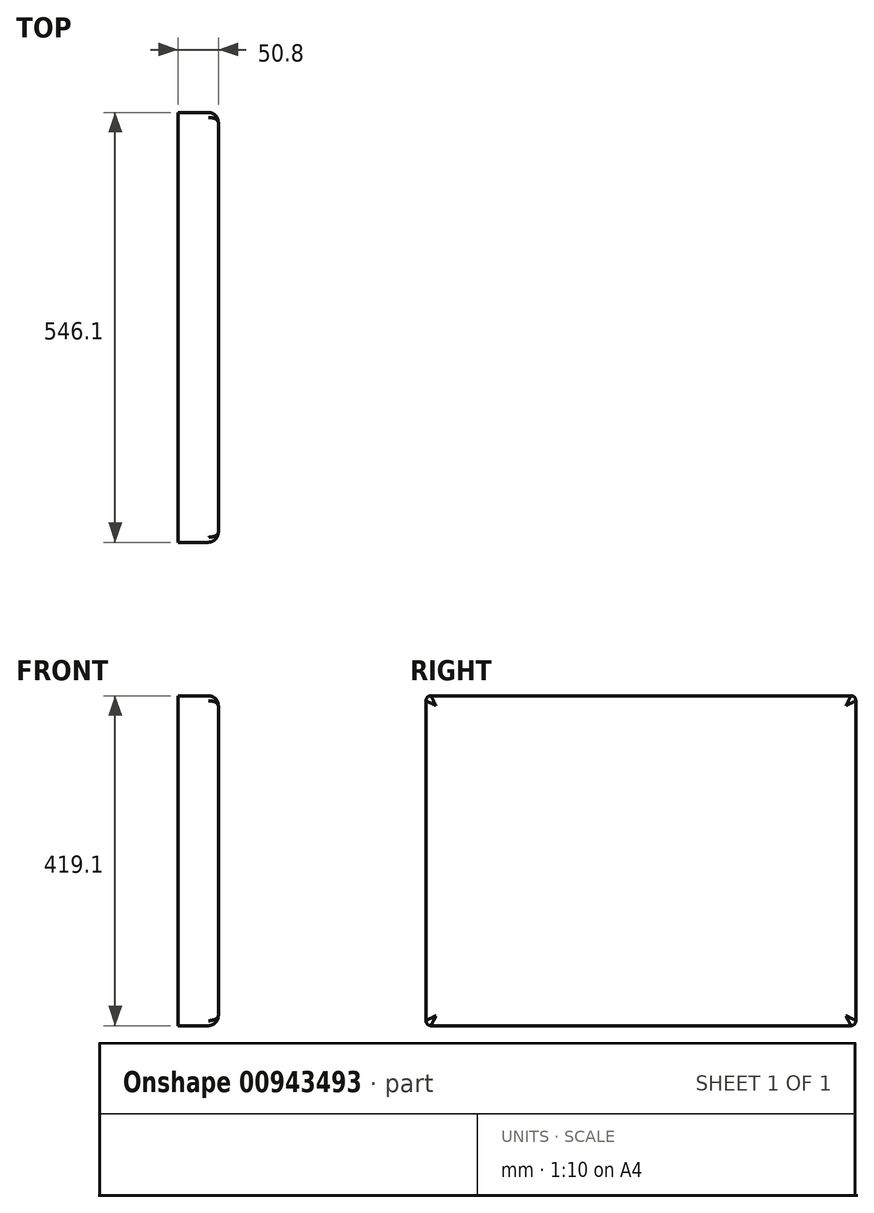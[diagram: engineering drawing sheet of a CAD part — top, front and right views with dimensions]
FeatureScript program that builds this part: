
annotation { "Feature Type Name" : "Feature", "Feature Type Description" : "" }
export const myFeature = defineFeature(function(context is Context, id is Id, definition is map)
    precondition{}
    {
        {
            var Q0;
            Q0=qCreatedBy(makeId("Right.planeOp"),FACE);
            var sketch = newSketch(context, id + "F0", { "sketchPlane" : qUnion([Q0])});
            skLineSegment(sketch, "E0.bottom", {"start": v(489.07, 13.05) * mm, "end": v(-44.33, 13.05) * mm});
            skLineSegment(sketch, "E0.top", {"start": v(489.07, 432.15) * mm, "end": v(-44.33, 432.15) * mm});
            skLineSegment(sketch, "E0.left", {"start": v(495.42, 19.4) * mm, "end": v(495.42, 425.8) * mm});
            skLineSegment(sketch, "E0.right", {"start": v(-50.68, 19.4) * mm, "end": v(-50.68, 425.8) * mm});
            skPoint(sketch, "E0.middle", {"position": v(222.37, 222.6) * mm});
            skLineSegment(sketch, "E1", {"start": v(-35.22, 13.05) * mm, "end": v(-29.34, 13.05) * mm});
            skPoint(sketch, "E2.visualSharp", {"position": v(-50.68, 13.05) * mm});
            skArc(sketch, "E2.filletArc", {"start": v(-50.68, 19.4) * mm, "mid": v(-48.82, 14.91) * mm, "end": v(-44.33, 13.05) * mm});
            skPoint(sketch, "E3.visualSharp", {"position": v(495.42, 13.05) * mm});
            skArc(sketch, "E3.filletArc", {"start": v(489.07, 13.05) * mm, "mid": v(493.56, 14.91) * mm, "end": v(495.42, 19.4) * mm});
            skPoint(sketch, "E4.visualSharp", {"position": v(495.42, 432.15) * mm});
            skArc(sketch, "E4.filletArc", {"start": v(495.42, 425.8) * mm, "mid": v(493.56, 430.3) * mm, "end": v(489.07, 432.15) * mm});
            skPoint(sketch, "E5.visualSharp", {"position": v(-50.68, 432.15) * mm});
            skArc(sketch, "E5.filletArc", {"start": v(-44.33, 432.15) * mm, "mid": v(-48.82, 430.3) * mm, "end": v(-50.68, 425.8) * mm});
            skSolve(sketch);
        }
        {
            var Q0;
            Q0=makeQuery(id+"F0.imprint","IMPRINT",FACE,{"disambiguationData":[TD([[makeQuery(id+"F0.imprint","IMPRINT",EDGE,{"derivedFrom":sQuery(id+"F0.wireOp",EDGE,"E0.top")}),1.0]])]});
            extrude(context, id + "F1", {"entities" : qUnion([Q0]), "depth" : 50.8 * mm, "offsetDistance" : 25.4 * mm});
        }
        {
            var Q0;
            Q0=makeQuery(id+"F1.opExtrude","CAP_EDGE",EDGE,{"disambiguationData":[OSD([sQuery(id+"F0.wireOp",EDGE,"E0.right")])],"isStart":false});
            var Q1;
            Q1=makeQuery(id+"F1.opExtrude","CAP_EDGE",EDGE,{"disambiguationData":[OSD([sQuery(id+"F0.wireOp",EDGE,"E0.top")])],"isStart":false});
            var Q2;
            Q2=makeQuery(id+"F1.opExtrude","CAP_EDGE",EDGE,{"disambiguationData":[OSD([sQuery(id+"F0.wireOp",EDGE,"E0.bottom"),sQuery(id+"F0.wireOp",EDGE,"E1")])],"isStart":false});
            var Q3;
            Q3=makeQuery(id+"F1.opExtrude","CAP_EDGE",EDGE,{"disambiguationData":[OSD([sQuery(id+"F0.wireOp",EDGE,"E0.left")])],"isStart":false});
            fillet(context, id + "F2", {"entities" : qUnion([Q0, Q1, Q2, Q3]), "radius" : 12.7 * mm, "tangentPropagation" : true, "allowEdgeOverflow" : false});
        }
    });
